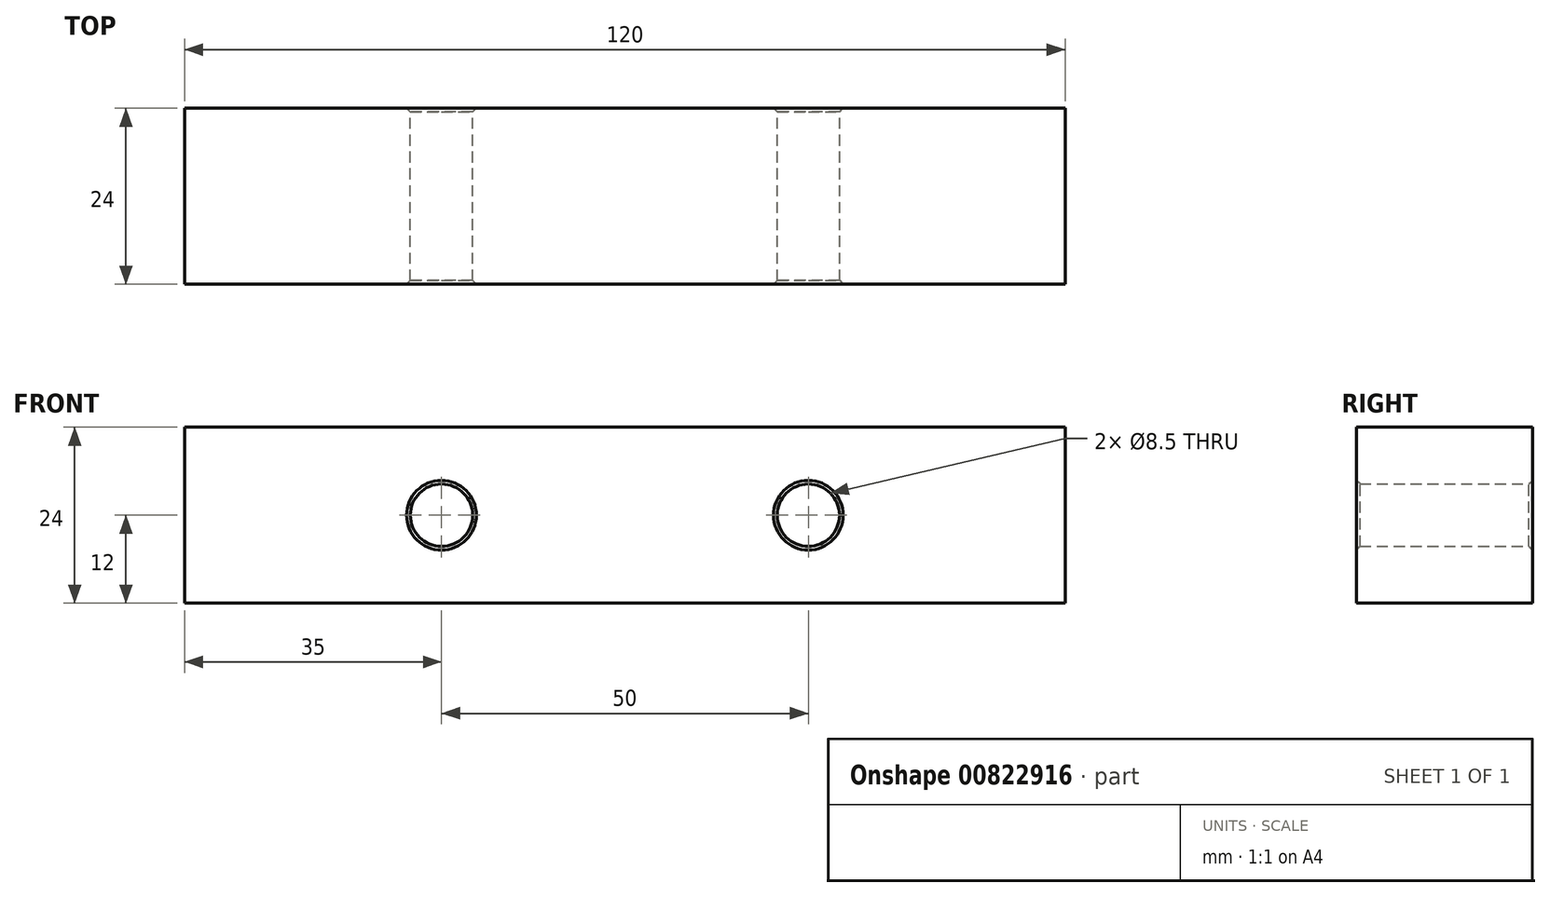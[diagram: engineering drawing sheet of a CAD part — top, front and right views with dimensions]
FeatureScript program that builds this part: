
annotation { "Feature Type Name" : "Feature", "Feature Type Description" : "" }
export const myFeature = defineFeature(function(context is Context, id is Id, definition is map)
    precondition{}
    {
        {
            var Q0;
            Q0=qCreatedBy(makeId("Front.planeOp"),FACE);
            var sketch = newSketch(context, id + "F0", { "sketchPlane" : qUnion([Q0])});
            skLineSegment(sketch, "E0.bottom", {"start": v(-60, -12) * mm, "end": v(60, -12) * mm});
            skLineSegment(sketch, "E0.top", {"start": v(-60, 12) * mm, "end": v(60, 12) * mm});
            skLineSegment(sketch, "E0.left", {"start": v(-60, -12) * mm, "end": v(-60, 12) * mm});
            skLineSegment(sketch, "E0.right", {"start": v(60, -12) * mm, "end": v(60, 12) * mm});
            skPoint(sketch, "E0.middle", {"position": v(0, 0) * mm});
            skLineSegment(sketch, "E1", {"start": v(0, 0) * mm, "end": v(-25, 0) * mm, "construction": true});
            skCircle(sketch, "E2", {"center": v(-25, 0) * mm, "radius": 4.25 * mm});
            skLineSegment(sketch, "E3", {"start": v(0, 0) * mm, "end": v(0, 81) * mm, "construction": true});
            skCircle(sketch, "E4.MirrorC", {"center": v(25, 0) * mm, "radius": 4.25 * mm});
            skSolve(sketch);
        }
        {
            var Q0;
            Q0 = qSketchRegion(id + "F0", true);
            extrude(context, id + "F1", {"entities" : qUnion([Q0]), "depth" : 24 * mm, "offsetDistance" : 25 * mm});
        }
        {
            var Q0;
            Q0=makeQuery(id+"F1.opExtrude","SWEPT_FACE",FACE,{"disambiguationData":[OSD([sQuery(id+"F0.wireOp",EDGE,"E2")])]});
            var Q1;
            Q1=makeQuery(id+"F1.opExtrude","SWEPT_FACE",FACE,{"disambiguationData":[OSD([sQuery(id+"F0.wireOp",EDGE,"E4.MirrorC")])]});
            chamfer(context, id + "F2", {"entities" : qUnion([Q0, Q1]), "width" : 0.5 * mm, "tangentPropagation" : true});
        }
    });
